# Revit family: MD2-ALTO
name_source: partatom
category: Lighting Fixtures
units: mm (PartAtom-declared; Revit-internal decimal feet)

## family parameters
Always vertical = Yes
Cut with Voids When Loaded = No
Host = Ceiling
Light Source = Yes
Maintain Annotation Orientation = No
OmniClass Number = 23.80.70.11.14.17
OmniClass Title = Direct/Indirect
Part Type = Normal
Room Calculation Point = No
Round Connector Dimension = Use Diameter
Shared = No

## types (16) — shared parameters
Assembly Code = D5020200
Color Filter = 16777215
Default Elevation = 0' - 0"
Description = Patient Room Luminaire with Ambient, Exam Functions
Dimming Lamp Color Temperature Shift = <None>
Emit Shape Visible in Rendering = No
Emit from Rectangle Height = 0' - 0 5/8"
Emit from Rectangle Length = 3' - 11 3/4"
Emit from Rectangle Width = 1' - 11 3/4"
Housing Finish = Metal - Viscor - White
Lamp = LED
Length = 3' - 11 3/4"
Lens Depth = 0' - 0 5/8"
Lens Finish = Acrylic - Viscor - Frosted White
Manufacturer = CERTOLUX A DIVISION OF VISCOR
Model = MD2-ALT0
Tilt Angle = 90.00°
URL = https://viscor.com
Voltage = 120 V
Width = 1' - 11 3/4"

## per-type parameters (varying)
| type | Apparent Load | Lamp Wattage | Photometric Web File |
| MD2-ALTO2X4-LED840K030LUNV (AMBIENT ONLY) | 24 VA | 24 VA | MD2-ALTO2X4-LED840K030LUNV (AMBIENT ONLY).ies |
| MD2-ALTO2X4-LED840K036LUNV (AMBIENT ONLY) | 29 VA | 29 VA | MD2-ALTO2X4-LED840K036LUNV (AMBIENT ONLY).ies |
| MD2-ALTO2X4-LED840K040LUNV (AMBIENT ONLY) | 34 VA | 34 VA | MD2-ALTO2X4-LED840K040LUNV (AMBIENT ONLY).ies |
| MD2-ALTO2X4-LED840K050LUNV (AMBIENT ONLY) | 41 VA | 41 VA | MD2-ALTO2X4-LED840K050LUNV (AMBIENT ONLY).ies |
| MD2-ALTO2X4-LED840K036LUNV (EXAM ONLY) | 24 VA | 24 VA | MD2-ALTO2X4-LED840K036LUNV (EXAM ONLY).ies |
| MD2-ALTO2X4-LED840K040LUNV (EXAM ONLY) | 28 VA | 28 VA | MD2-ALTO2X4-LED840K040LUNV (EXAM ONLY).ies |
| MD2-ALTO2X4-LED840K050LUNV (EXAM ONLY) | 34 VA | 34 VA | MD2-ALTO2X4-LED840K050LUNV (EXAM ONLY).ies |
| MD2-ALTO2X4-LED840K060LUNV (EXAM ONLY) | 41 VA | 41 VA | MD2-ALTO2X4-LED840K060LUNV (EXAM ONLY).ies |
| MD2-ALTO2X4-LED840K070LUNV (EXAM ONLY) | 48 VA | 48 VA | MD2-ALTO2X4-LED840K070LUNV (EXAM ONLY).ies |
| MD2-ALTO2X4-LED840K030L_036LUNV (AMBIENT + EXAM ON) | 48 VA | 48 VA | MD2-ALTO2X4-LED840K030L_036LUNV (AMBIENT + EXAM ON).ies |
| MD2-ALTO2X4-LED840K036L_036LUNV (AMBIENT + EXAM ON) | 53 VA | 53 VA | MD2-ALTO2X4-LED840K036L_036LUNV (AMBIENT + EXAM ON).ies |
| MD2-ALTO2X4-LED840K040L_040LUNV (AMBIENT + EXAM ON) | 62 VA | 62 VA | MD2-ALTO2X4-LED840K040L_040LUNV (AMBIENT + EXAM ON).ies |
| MD2-ALTO2X4-LED840K040L_050LUNV (AMBIENT + EXAM ON) | 68 VA | 68 VA | MD2-ALTO2X4-LED840K040L_050LUNV (AMBIENT + EXAM ON).ies |
| MD2-ALTO2X4-LED840K040L_060LUNV  (AMBIENT + EXAM ON) | 75 VA | 75 VA | MD2-ALTO2X4-LED840K040L_060LUNV  (AMBIENT + EXAM ON).ies |
| MD2-ALTO2X4-LED840K050L_060LUNV (AMBIENT + EXAM ON) | 82 VA | 82 VA | MD2-ALTO2X4-LED840K050L_060LUNV (AMBIENT + EXAM ON).ies |
| MD2-ALTO2X4-LED840K050L_070LUNV (AMBIENT + EXAM ON) | 89 VA | 89 VA | MD2-ALTO2X4-LED840K050L_070LUNV (AMBIENT + EXAM ON).ies |

## geometry (parser evidence)
native form markers: Sweep x2
no freeform markers — native parametric forms only
